# Revit family: Walkway_Kattsafe_Fibre
name_source: partatom
category: Specialty Equipment
units: mm (PartAtom-declared; Revit-internal decimal feet)

## family parameters
Cut with Voids When Loaded = No
Enable Cutting in Views = No
Maintain Annotation Orientation = No
OmniClass Number = 23.13.41.19
Part Type = Normal
Room Calculation Point = No
Round Connector Dimension = Use Diameter
Shared = No

## types (2) — shared parameters
Assembly Code = E1090100
BattenMaterial = Aluminum_Kattsafe_Satin
Description = Kattsafe guardrail systems are the preferred method of safe access across roofs and areas close to a fall edge. The system requires no specialist PPE, personnel or training to safely prevent a fall with a walkway to designate a safe path of access across the roof surface.
EdgebarMaterial = Resin_Kattsafe_Yellow
ElementType = Roof Walkway
Export Type to IFC As = IfcBuildingElementProxy
IfcExportAs = IfcBuildingElementProxy
IfcExportType = USERDEFINED
Manufacturer = Kattsafe®
ManufacturerOverallWidth = 615 mm  [stored 2.01772 ft]
ManufacturerURLProductSpecific = https://kattsafe.com.au
ModifiedIssue = 20240430 $
Type IFC Predefined Type = USERDEFINED
URL = https://kattsafe.com.au
Uniclass2015Code = Pr_40_70_75_96
Uniclass2015Title = Working platforms
Uniclass2015Version = Products v1.23
WalkwayMaterial = Resin_Kattsafe_Mesh_Yellow
WalkwayWidth = 615 mm  [stored 2.01772 ft]
zero-valued in all types: Default Elevation

## per-type parameters (varying)
| type | Battens | ManufacturerOverallHeight | ManufacturerSpecCode | Model | Type Comments |
| Without Battens (GW364Y) | No | 15 mm  [stored 0.0492126 ft] | GW364Y | GW364Y | Fibre Walkway |
| With Battens (GW13) | Yes | 55 mm  [stored 0.180446 ft] | GW13 | GW13 | Fibre Walkway - On Battens |

note: [stored X ft] marks values corroborated as IEEE doubles in the binary element streams (Revit-internal decimal feet)

## geometry (parser evidence)
native form markers: Sweep x11
no freeform markers — native parametric forms only
